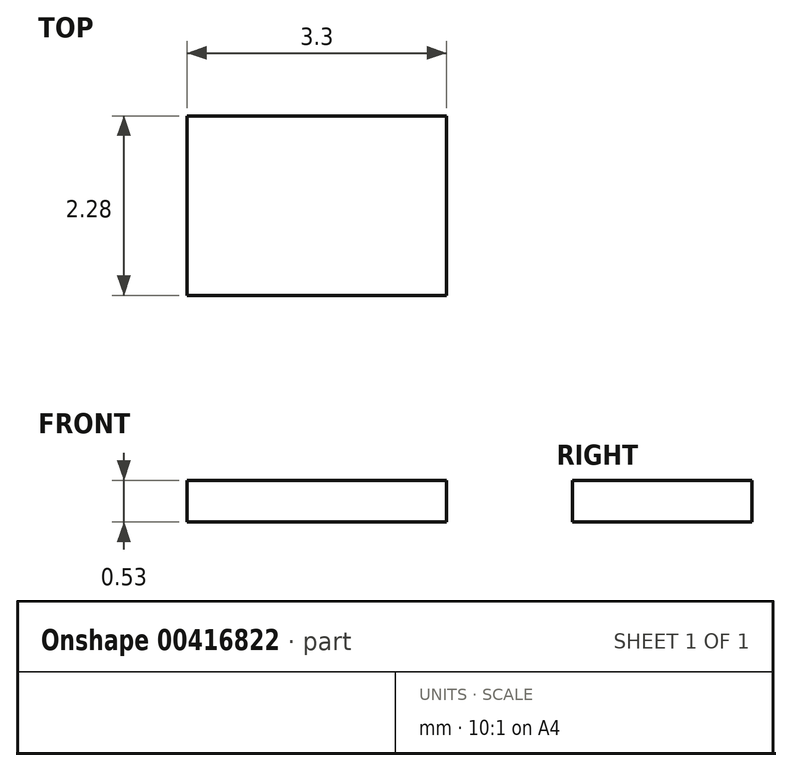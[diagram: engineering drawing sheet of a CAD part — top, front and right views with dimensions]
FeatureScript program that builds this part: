
annotation { "Feature Type Name" : "Feature", "Feature Type Description" : "" }
export const myFeature = defineFeature(function(context is Context, id is Id, definition is map)
    precondition{}
    {
        {
            var Q0;
            Q0=qCreatedBy(makeId("Top.planeOp"),FACE);
            var sketch = newSketch(context, id + "F0", { "sketchPlane" : qUnion([Q0])});
            skLineSegment(sketch, "E0.bottom", {"start": v(0, 0) * mm, "end": v(3.3, 0) * mm});
            skLineSegment(sketch, "E0.top", {"start": v(0, 2.28) * mm, "end": v(3.3, 2.28) * mm});
            skLineSegment(sketch, "E0.left", {"start": v(0, 0) * mm, "end": v(0, 2.28) * mm});
            skLineSegment(sketch, "E0.right", {"start": v(3.3, 0) * mm, "end": v(3.3, 2.28) * mm});
            skSolve(sketch);
        }
        {
            var Q0;
            Q0 = qSketchRegion(id + "F0", true);
            extrude(context, id + "F1", {"entities" : qUnion([Q0]), "depth" : .53 * mm, "offsetDistance" : 25.4 * mm});
        }
    });
